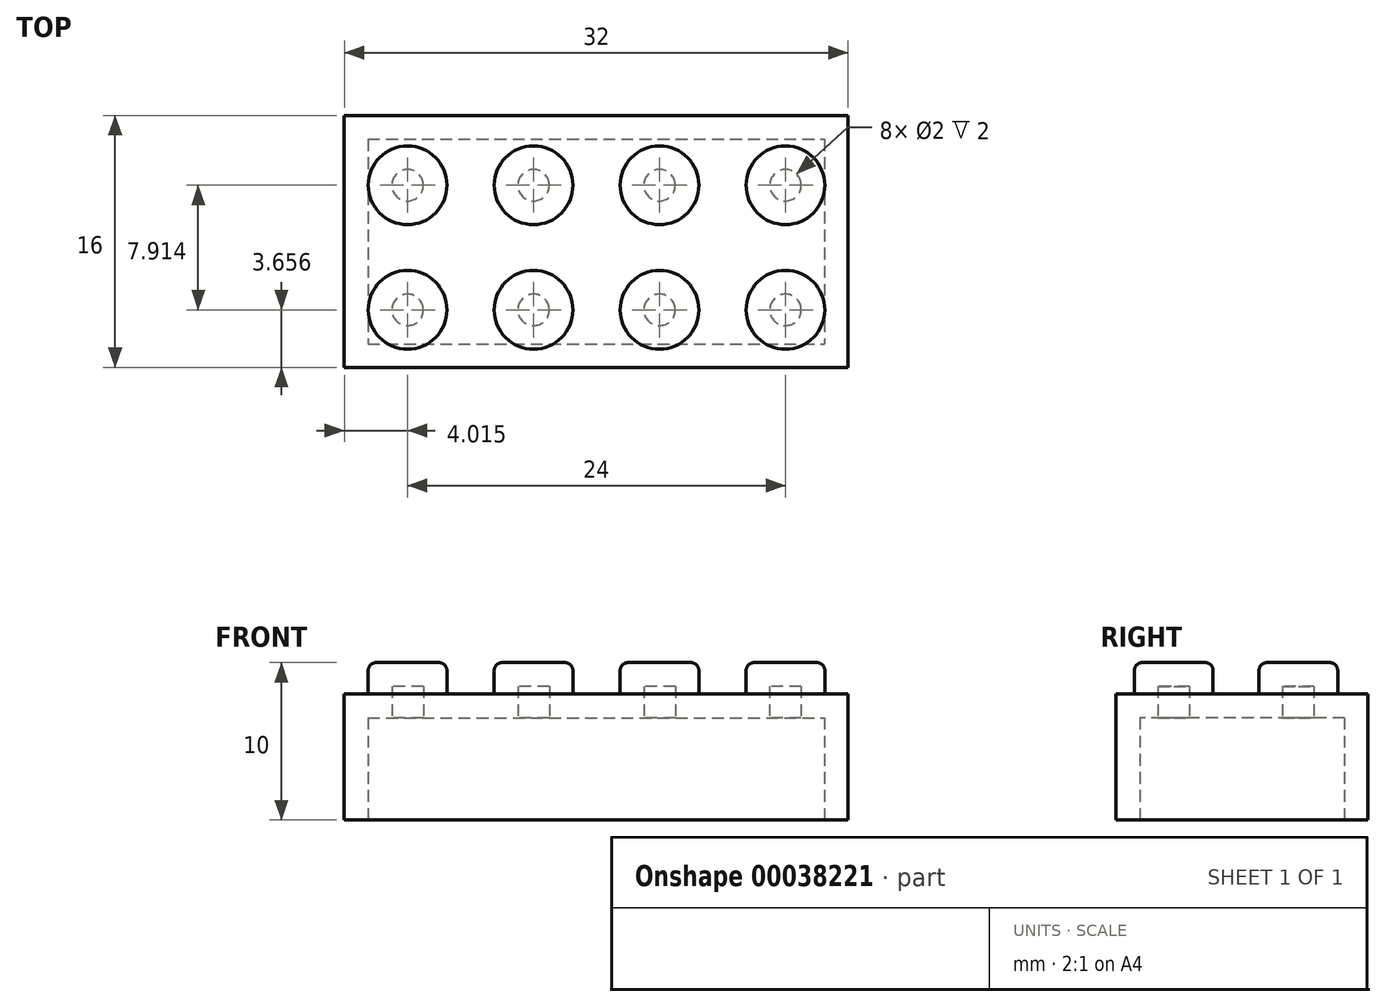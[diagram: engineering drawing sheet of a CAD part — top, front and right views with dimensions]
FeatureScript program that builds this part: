
annotation { "Feature Type Name" : "Feature", "Feature Type Description" : "" }
export const myFeature = defineFeature(function(context is Context, id is Id, definition is map)
    precondition{}
    {
        {
            var Q0;
            Q0=qCreatedBy(makeId("Top.planeOp"),FACE);
            var sketch = newSketch(context, id + "F0", { "sketchPlane" : qUnion([Q0])});
            skLineSegment(sketch, "E0.bottom", {"start": v(-13.75, 4.43) * mm, "end": v(18.25, 4.43) * mm});
            skLineSegment(sketch, "E0.top", {"start": v(-13.75, -11.57) * mm, "end": v(18.25, -11.57) * mm});
            skLineSegment(sketch, "E0.left", {"start": v(-13.75, 4.43) * mm, "end": v(-13.75, -11.57) * mm});
            skLineSegment(sketch, "E0.right", {"start": v(18.25, 4.43) * mm, "end": v(18.25, -11.57) * mm});
            skSolve(sketch);
        }
        {
            var Q0;
            Q0=makeQuery(id+"F0.imprint","IMPRINT",FACE,{"disambiguationData":[TD([[makeQuery(id+"F0.imprint","IMPRINT",EDGE,{"derivedFrom":sQuery(id+"F0.wireOp",EDGE,"E0.bottom")}),-1.0]])]});
            extrude(context, id + "F1", {"entities" : qUnion([Q0]), "depth" : 8 * mm});
        }
        {
            var Q0;
            Q0=qCreatedBy(makeId("Top.planeOp"),FACE);
            cPlane(context, id + "F2", {"entities" : qUnion([Q0]), "cplaneType" : CPlaneType.OFFSET, "offset" : 8 * mm, "width" : 150 * mm, "height" : 150 * mm});
        }
        {
            var Q0;
            Q0=qCreatedBy(id+"F2.planeOp",FACE);
            var sketch = newSketch(context, id + "F3", { "sketchPlane" : qUnion([Q0])});
            skCircle(sketch, "E1", {"center": v(-9.73, 0) * mm, "radius": 2.5 * mm});
            skCircle(sketch, "E2", {"center": v(-1.73, 0) * mm, "radius": 2.5 * mm});
            skCircle(sketch, "E3", {"center": v(6.27, 0) * mm, "radius": 2.5 * mm});
            skCircle(sketch, "E4", {"center": v(14.27, 0) * mm, "radius": 2.5 * mm});
            skCircle(sketch, "E5", {"center": v(14.27, -7.91) * mm, "radius": 2.5 * mm});
            skCircle(sketch, "E6", {"center": v(6.27, -7.91) * mm, "radius": 2.5 * mm});
            skCircle(sketch, "E7", {"center": v(-1.73, -7.91) * mm, "radius": 2.5 * mm});
            skCircle(sketch, "E8", {"center": v(-9.73, -7.91) * mm, "radius": 2.5 * mm});
            skLineSegment(sketch, "E9", {"start": v(-13.73, 4.46) * mm, "end": v(-9.73, 4.46) * mm, "construction": true});
            skLineSegment(sketch, "E10", {"start": v(-9.73, 4.46) * mm, "end": v(-1.73, 4.46) * mm, "construction": true});
            skLineSegment(sketch, "E11", {"start": v(-1.73, 4.46) * mm, "end": v(6.27, 4.46) * mm, "construction": true});
            skLineSegment(sketch, "E12", {"start": v(6.27, 4.46) * mm, "end": v(14.27, 4.46) * mm, "construction": true});
            skLineSegment(sketch, "E13", {"start": v(14.27, 4.46) * mm, "end": v(18.27, 4.46) * mm, "construction": true});
            skLineSegment(sketch, "E14", {"start": v(-13.73, 4.46) * mm, "end": v(-13.73, 0) * mm, "construction": true});
            skLineSegment(sketch, "E15", {"start": v(-13.73, 0) * mm, "end": v(-13.73, -3.9) * mm, "construction": true});
            skLineSegment(sketch, "E16", {"start": v(-13.73, -3.9) * mm, "end": v(-13.73, -7.91) * mm, "construction": true});
            skLineSegment(sketch, "E17", {"start": v(-13.73, -7.91) * mm, "end": v(-13.73, -11.5) * mm, "construction": true});
            skSolve(sketch);
        }
        {
            var Q0;
            Q0=makeQuery(id+"F3.imprint","IMPRINT",FACE,{"disambiguationData":[TD([[makeQuery(id+"F3.imprint","IMPRINT",EDGE,{"derivedFrom":sQuery(id+"F3.wireOp",EDGE,"E4")}),1.0]])]});
            var Q1;
            Q1=makeQuery(id+"F3.imprint","IMPRINT",FACE,{"disambiguationData":[TD([[makeQuery(id+"F3.imprint","IMPRINT",EDGE,{"derivedFrom":sQuery(id+"F3.wireOp",EDGE,"E5")}),1.0]])]});
            var Q2;
            Q2=makeQuery(id+"F3.imprint","IMPRINT",FACE,{"disambiguationData":[TD([[makeQuery(id+"F3.imprint","IMPRINT",EDGE,{"derivedFrom":sQuery(id+"F3.wireOp",EDGE,"E6")}),1.0]])]});
            var Q3;
            Q3=makeQuery(id+"F3.imprint","IMPRINT",FACE,{"disambiguationData":[TD([[makeQuery(id+"F3.imprint","IMPRINT",EDGE,{"derivedFrom":sQuery(id+"F3.wireOp",EDGE,"E3")}),1.0]])]});
            var Q4;
            Q4=makeQuery(id+"F3.imprint","IMPRINT",FACE,{"disambiguationData":[TD([[makeQuery(id+"F3.imprint","IMPRINT",EDGE,{"derivedFrom":sQuery(id+"F3.wireOp",EDGE,"E2")}),1.0]])]});
            var Q5;
            Q5=makeQuery(id+"F3.imprint","IMPRINT",FACE,{"disambiguationData":[TD([[makeQuery(id+"F3.imprint","IMPRINT",EDGE,{"derivedFrom":sQuery(id+"F3.wireOp",EDGE,"E7")}),1.0]])]});
            var Q6;
            Q6=makeQuery(id+"F3.imprint","IMPRINT",FACE,{"disambiguationData":[TD([[makeQuery(id+"F3.imprint","IMPRINT",EDGE,{"derivedFrom":sQuery(id+"F3.wireOp",EDGE,"E8")}),1.0]])]});
            var Q7;
            Q7=makeQuery(id+"F3.imprint","IMPRINT",FACE,{"disambiguationData":[TD([[makeQuery(id+"F3.imprint","IMPRINT",EDGE,{"derivedFrom":sQuery(id+"F3.wireOp",EDGE,"E1")}),1.0]])]});
            extrude(context, id + "F4", {"entities" : qUnion([Q0, Q1, Q2, Q3, Q4, Q5, Q6, Q7]), "operationType" : NewBodyOperationType.ADD, "depth" : 2 * mm});
        }
        {
            var Q0;
            Q0=makeQuery(id+"F4.opExtrude","CAP_FACE",FACE,{"disambiguationData":[OSD([sQuery(id+"F3.wireOp",EDGE,"E5")])],"isStart":false});
            var Q1;
            Q1=makeQuery(id+"F4.opExtrude","CAP_FACE",FACE,{"disambiguationData":[OSD([sQuery(id+"F3.wireOp",EDGE,"E4")])],"isStart":false});
            var Q2;
            Q2=makeQuery(id+"F4.opExtrude","CAP_FACE",FACE,{"disambiguationData":[OSD([sQuery(id+"F3.wireOp",EDGE,"E3")])],"isStart":false});
            var Q3;
            Q3=makeQuery(id+"F4.opExtrude","CAP_FACE",FACE,{"disambiguationData":[OSD([sQuery(id+"F3.wireOp",EDGE,"E6")])],"isStart":false});
            var Q4;
            Q4=makeQuery(id+"F4.opExtrude","CAP_FACE",FACE,{"disambiguationData":[OSD([sQuery(id+"F3.wireOp",EDGE,"E7")])],"isStart":false});
            var Q5;
            Q5=makeQuery(id+"F4.opExtrude","CAP_FACE",FACE,{"disambiguationData":[OSD([sQuery(id+"F3.wireOp",EDGE,"E2")])],"isStart":false});
            var Q6;
            Q6=makeQuery(id+"F4.opExtrude","CAP_FACE",FACE,{"disambiguationData":[OSD([sQuery(id+"F3.wireOp",EDGE,"E1")])],"isStart":false});
            var Q7;
            Q7=makeQuery(id+"F4.opExtrude","CAP_FACE",FACE,{"disambiguationData":[OSD([sQuery(id+"F3.wireOp",EDGE,"E8")])],"isStart":false});
            fillet(context, id + "F5", {"entities" : qUnion([Q0, Q1, Q2, Q3, Q4, Q5, Q6, Q7]), "radius" : 0.5 * mm, "tangentPropagation" : true, "allowEdgeOverflow" : false});
        }
        {
            var Q0;
            Q0=makeQuery(id+"F1.opExtrude","CAP_FACE",FACE,{"disambiguationData":[OSD([sQuery(id+"F0.wireOp",EDGE,"E0.bottom"),sQuery(id+"F0.wireOp",EDGE,"E0.top"),sQuery(id+"F0.wireOp",EDGE,"E0.left"),sQuery(id+"F0.wireOp",EDGE,"E0.right")])],"isStart":true});
            shell(context, id + "F6", {"entities" : qUnion([Q0]), "thickness" : 1.5 * mm});
        }
    });
